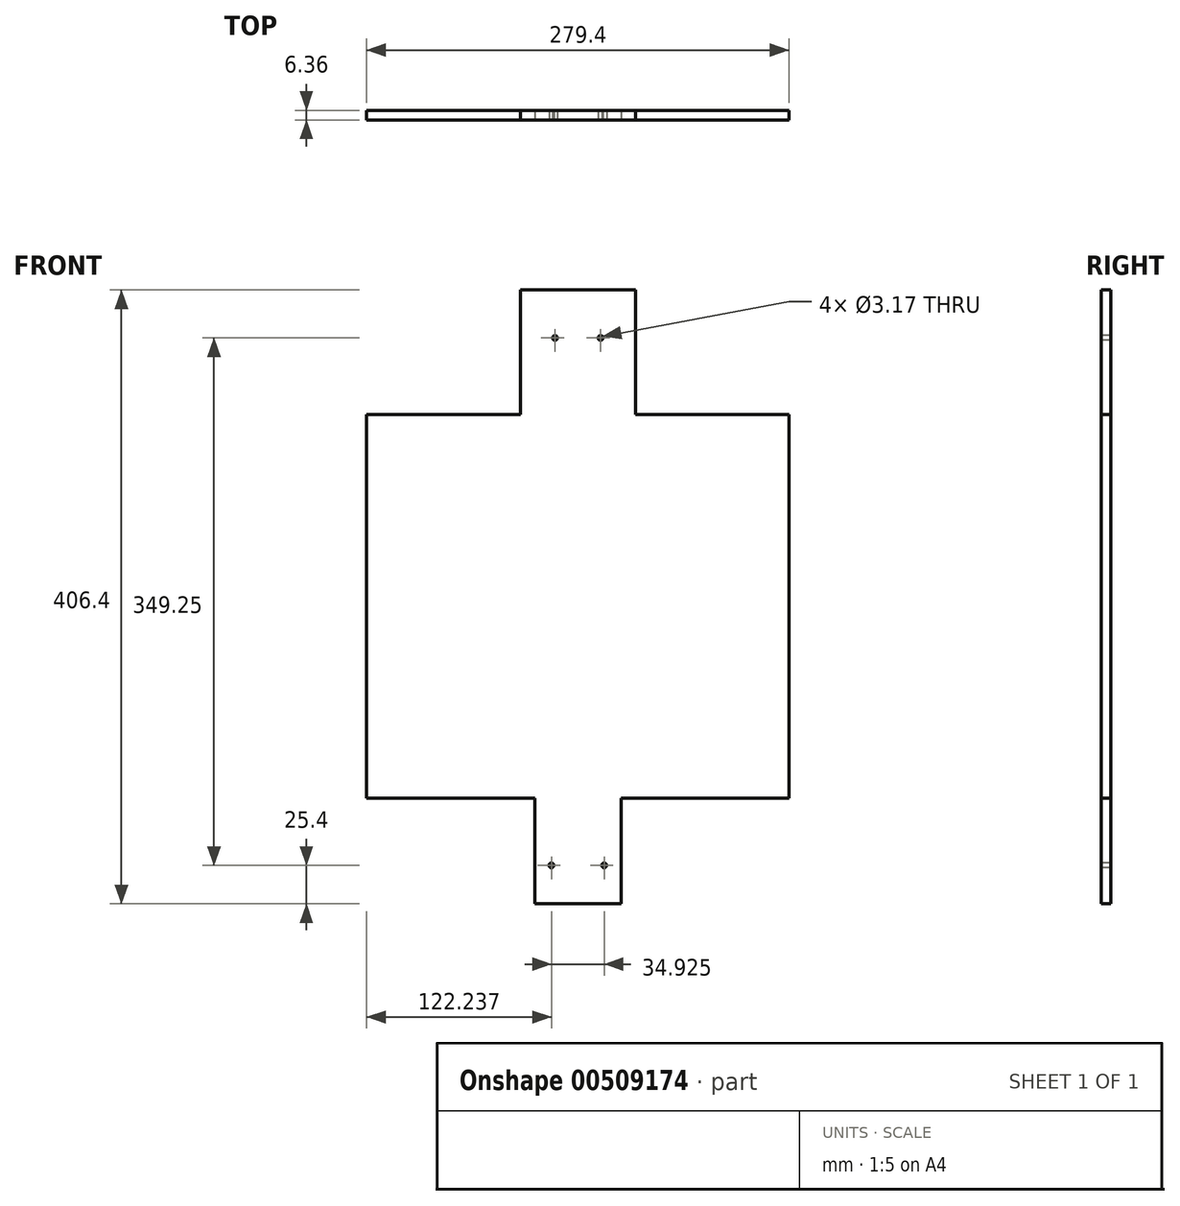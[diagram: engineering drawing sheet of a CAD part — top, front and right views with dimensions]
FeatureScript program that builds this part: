
annotation { "Feature Type Name" : "Feature", "Feature Type Description" : "" }
export const myFeature = defineFeature(function(context is Context, id is Id, definition is map)
    precondition{}
    {
        {
            var Q0;
            Q0=qCreatedBy(makeId("Top.planeOp"),FACE);
            var sketch = newSketch(context, id + "F0", { "sketchPlane" : qUnion([Q0])});
            skLineSegment(sketch, "E0.bottom", {"start": v(139.7, -3.17) * mm, "end": v(-139.7, -3.18) * mm});
            skLineSegment(sketch, "E0.top", {"start": v(139.7, 3.18) * mm, "end": v(-139.7, 3.18) * mm});
            skLineSegment(sketch, "E0.left", {"start": v(139.7, -3.17) * mm, "end": v(139.7, 3.18) * mm});
            skLineSegment(sketch, "E0.right", {"start": v(-139.7, -3.18) * mm, "end": v(-139.7, 3.17) * mm});
            skPoint(sketch, "E0.middle", {"position": v(0, 0) * mm});
            skSolve(sketch);
        }
        {
            var Q0;
            Q0 = qSketchRegion(id + "F0", true);
            extrude(context, id + "F1", {"entities" : qUnion([Q0]), "depth" : 127 * mm, "hasSecondDirection" : true, "secondDirectionOppositeDirection" : true, "secondDirectionDepth" : 127 * mm});
        }
        {
            var Q0;
            Q0=makeQuery(id+"F1.opExtrude","CAP_FACE",FACE,{"disambiguationData":[OSD([sQuery(id+"F0.wireOp",EDGE,"E0.bottom"),sQuery(id+"F0.wireOp",EDGE,"E0.top"),sQuery(id+"F0.wireOp",EDGE,"E0.left"),sQuery(id+"F0.wireOp",EDGE,"E0.right")])],"isStart":false});
            var sketch = newSketch(context, id + "F2", { "sketchPlane" : qUnion([Q0])});
            skLineSegment(sketch, "E1.bottom", {"start": v(38.1, -3.17) * mm, "end": v(-38.1, -3.17) * mm});
            skLineSegment(sketch, "E1.top", {"start": v(38.1, 3.17) * mm, "end": v(-38.1, 3.17) * mm});
            skLineSegment(sketch, "E1.left", {"start": v(38.1, -3.17) * mm, "end": v(38.1, 3.17) * mm});
            skLineSegment(sketch, "E1.right", {"start": v(-38.1, -3.18) * mm, "end": v(-38.1, 3.17) * mm});
            skPoint(sketch, "E1.middle", {"position": v(0, 0) * mm});
            skSolve(sketch);
        }
        {
            var Q0;
            Q0 = qSketchRegion(id + "F0", true);
            var Q1;
            Q1 = qSketchRegion(id + "F2", true);
            extrude(context, id + "F3", {"entities" : qUnion([Q0, Q1]), "operationType" : NewBodyOperationType.ADD, "depth" : 82.55 * mm});
        }
        {
            var Q0;
            Q0=makeQuery(id+"F1.opExtrude","CAP_FACE",FACE,{"disambiguationData":[OSD([sQuery(id+"F0.wireOp",EDGE,"E0.bottom"),sQuery(id+"F0.wireOp",EDGE,"E0.top"),sQuery(id+"F0.wireOp",EDGE,"E0.left"),sQuery(id+"F0.wireOp",EDGE,"E0.right")])],"isStart":true});
            var sketch = newSketch(context, id + "F4", { "sketchPlane" : qUnion([Q0])});
            skLineSegment(sketch, "E2.bottom", {"start": v(28.58, -3.18) * mm, "end": v(-28.58, -3.18) * mm});
            skLineSegment(sketch, "E2.top", {"start": v(28.58, 3.18) * mm, "end": v(-28.58, 3.18) * mm});
            skLineSegment(sketch, "E2.left", {"start": v(28.58, -3.18) * mm, "end": v(28.58, 3.18) * mm});
            skLineSegment(sketch, "E2.right", {"start": v(-28.58, -3.18) * mm, "end": v(-28.58, 3.18) * mm});
            skPoint(sketch, "E2.middle", {"position": v(0, 0) * mm});
            skSolve(sketch);
        }
        {
            var Q0;
            Q0 = qSketchRegion(id + "F4", true);
            extrude(context, id + "F5", {"entities" : qUnion([Q0]), "operationType" : NewBodyOperationType.ADD, "depth" : 69.85 * mm});
        }
        {
            var Q0;
            Q0=makeQuery(id+"F5.boolean.opBoolean","MERGE",FACE,{"derivedFrom":[makeQuery(id+"F3.boolean.opBoolean","MERGE",FACE,{"derivedFrom":[makeQuery(id+"F1.opExtrude","SWEPT_FACE",FACE,{"disambiguationData":[OSD([sQuery(id+"F0.wireOp",EDGE,"E0.bottom")])]}),makeQuery(id+"F3.opExtrude","SWEPT_FACE",FACE,{"disambiguationData":[OSD([sQuery(id+"F2.wireOp",EDGE,"E1.bottom")])]})]}),makeQuery(id+"F5.opExtrude","SWEPT_FACE",FACE,{"disambiguationData":[OSD([sQuery(id+"F4.wireOp",EDGE,"E2.top")])]})]});
            var sketch = newSketch(context, id + "F6", { "sketchPlane" : qUnion([Q0])});
            skCircle(sketch, "E3", {"center": v(-17.46, -171.45) * mm, "radius": 1.59 * mm});
            skCircle(sketch, "E4", {"center": v(17.46, -171.45) * mm, "radius": 1.59 * mm});
            skSolve(sketch);
        }
        {
            var Q0;
            Q0 = qSketchRegion(id + "F6", true);
            extrude(context, id + "F7", {"entities" : qUnion([Q0]), "operationType" : NewBodyOperationType.REMOVE, "endBound" : BoundingType.THROUGH_ALL, "oppositeDirection" : true, "depth" : 25.4 * mm});
        }
        {
            var Q0;
            Q0=makeQuery(id+"F5.boolean.opBoolean","MERGE",FACE,{"derivedFrom":[makeQuery(id+"F3.boolean.opBoolean","MERGE",FACE,{"derivedFrom":[makeQuery(id+"F1.opExtrude","SWEPT_FACE",FACE,{"disambiguationData":[OSD([sQuery(id+"F0.wireOp",EDGE,"E0.bottom")])]}),makeQuery(id+"F3.opExtrude","SWEPT_FACE",FACE,{"disambiguationData":[OSD([sQuery(id+"F2.wireOp",EDGE,"E1.bottom")])]})]}),makeQuery(id+"F5.opExtrude","SWEPT_FACE",FACE,{"disambiguationData":[OSD([sQuery(id+"F4.wireOp",EDGE,"E2.top")])]})]});
            var sketch = newSketch(context, id + "F8", { "sketchPlane" : qUnion([Q0])});
            skCircle(sketch, "E5", {"center": v(-15.08, 177.8) * mm, "radius": 1.59 * mm});
            skCircle(sketch, "E6", {"center": v(15.08, 177.8) * mm, "radius": 1.59 * mm});
            skSolve(sketch);
        }
        {
            var Q0;
            Q0 = qSketchRegion(id + "F8", true);
            extrude(context, id + "F9", {"entities" : qUnion([Q0]), "operationType" : NewBodyOperationType.REMOVE, "endBound" : BoundingType.THROUGH_ALL, "oppositeDirection" : true, "depth" : 25.4 * mm});
        }
    });
